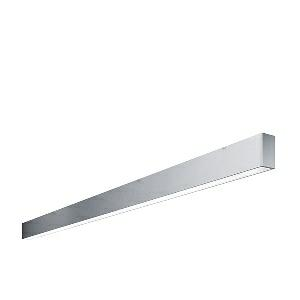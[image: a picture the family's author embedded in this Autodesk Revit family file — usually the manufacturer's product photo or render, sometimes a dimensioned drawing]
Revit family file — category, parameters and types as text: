
# Revit family: dotoo_line_-_dla_3000_840_d_end_00807960_af9d
name_source: partatom
category: Lighting Fixtures
units: mm (PartAtom-declared; Revit-internal decimal feet)

## family parameters
Cut with Voids When Loaded = No
Host = Face
Light Source = No
Part Type = Normal
Room Calculation Point = No
Round Connector Dimension = Use Diameter
Shared = No

## types (1)
- DOTOO.line - DLA 3000/840/D END (1 x LED, 2750 lm, 4000K)
    Apparent Load = 26 VA
    Approval mark = CE
    CIE Flux Codes = 67 91 98 100 100
    Color Rendering = 80-89
    Color Temperature = 4000K
    Control Gear = Electronic ballast
    Default Elevation = 1800 mm
    Description = DLA 3000/840/D|Surface-mounted luminaire.|light source: LED|work equipment: Adjustable electronic ballast, digital DALI|connected load: 220-240 V, 50/60 Hz|Power consumption: approx. 26 W|luminous flux: 2750 lm|luminous efficacy: 105 lm/W|light distribution: Direct|colour temperature: Cold white, ca. 4000 K|class of protection: I|technology: Continuously dimmable|mains lead: Connector|glare control: Prism aperture|special features: DALI Load 1x, TouchDIM - dimming via standard switch, Through-wired, up to 18 m on one mains connection, Flicker-free, Suitable as emergency lighting, Mechanical and electrical connection of the individual modules without tools|
    Frequency = 50 Hz
    Height = 110 mm
    Lamp = 1 x LED
    Lamp Light Flux = 2750 lm
    Lamp count = 1
    Length = 2250 mm
    Luminous efficacy = 106 lm/W
    Manufacturer = Waldmann
    ModVariant = No
    Model = 00807960
    Mounting Place = Ceiling
    Mounting Type = Surface mounted
    Number of Poles = 1
    OnlyDefault = Yes
    Power Factor = 1
    Product Name = DOTOO.line - DLA 3000/840/D END
    Product group = Ceiling mounted luminaire
    ProductGroupID = 3
    Protection Class = Protection class I
    Protection Degree = IP 40
    RLX_Detail_Level = 1
    RLX_Emergency_Light_Flux = 0 lm
    RLX_Emergency_Type = 0
    RLX_Emergency_Type_DB = No
    RlxData = <blob elided: 21021 chars, md5=b2bfe88c>
    Socket = socket
    Standby Power = 0 W
    System Light Flux = 2750 lm
    System Power = 26 W
    Type Comments = Product without accessories
    Type Image = 114383000-00807960.jpg
    URL = http://relux.com
    VarID = ---
    Voltage = 230 V
    Voltage Range = 220-240 V
    Weight = 0.00 kg
    Width = 60 mm  [stored 0.19685 ft]

note: [stored X ft] marks values corroborated as IEEE doubles in the binary element streams (Revit-internal decimal feet)

## geometry (parser evidence)
native form markers: Blend x4, Sweep x13
no freeform markers — native parametric forms only
